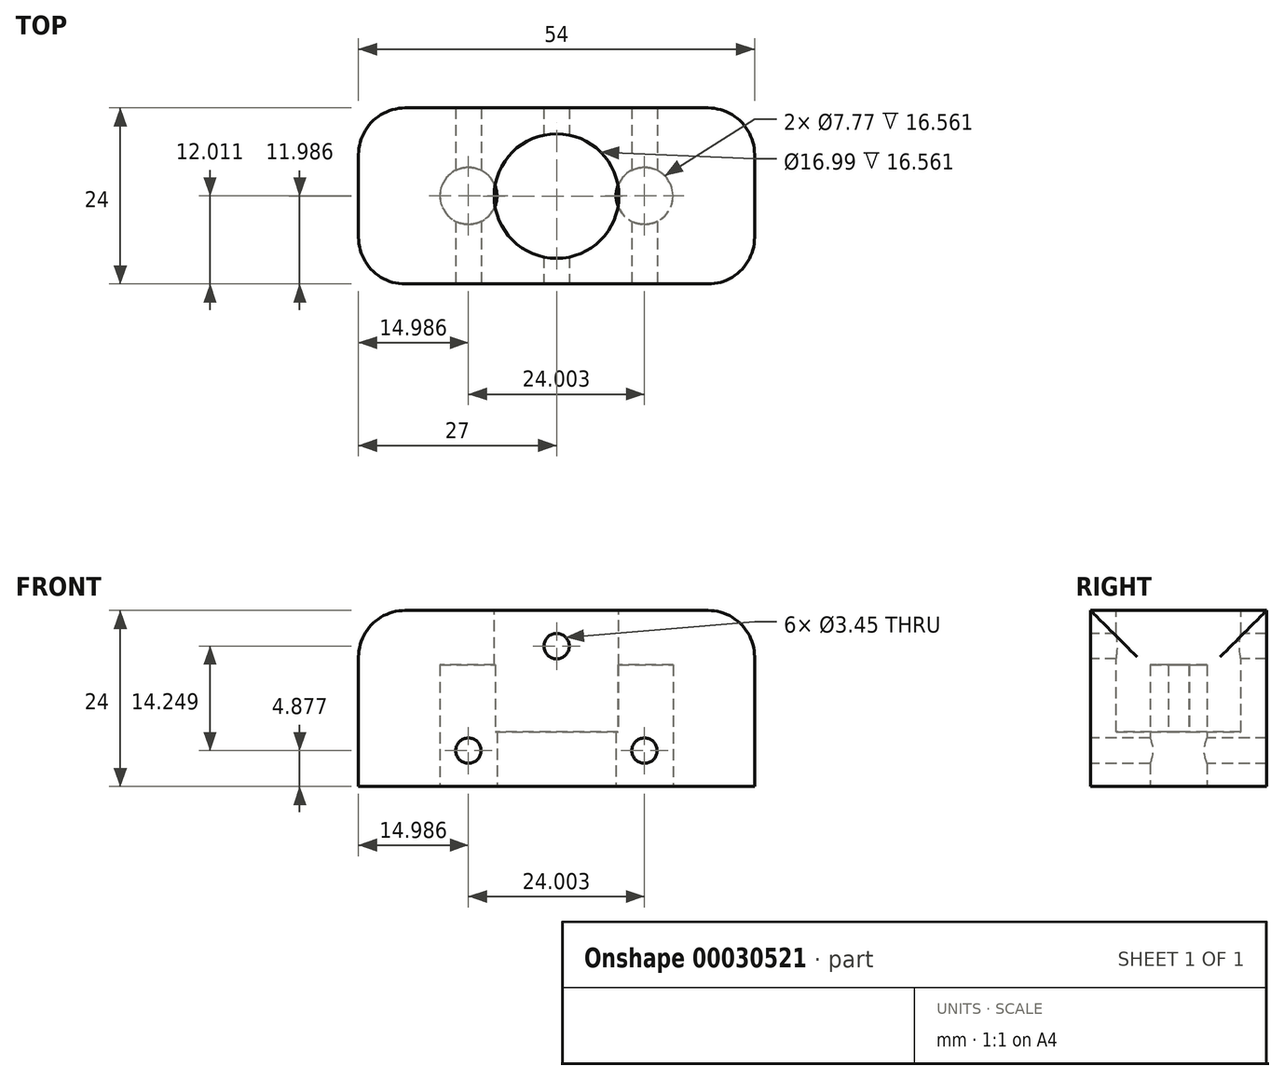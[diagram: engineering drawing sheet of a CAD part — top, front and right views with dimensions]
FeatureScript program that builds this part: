
annotation { "Feature Type Name" : "Feature", "Feature Type Description" : "" }
export const myFeature = defineFeature(function(context is Context, id is Id, definition is map)
    precondition{}
    {
        {
            var Q0;
            Q0=qCreatedBy(makeId("Front.planeOp"),FACE);
            var sketch = newSketch(context, id + "F0", { "sketchPlane" : qUnion([Q0])});
            skLineSegment(sketch, "E0.bottom", {"start": v(0, 0) * mm, "end": v(54, 0) * mm});
            skLineSegment(sketch, "E0.top", {"start": v(0, 24) * mm, "end": v(54, 24) * mm});
            skLineSegment(sketch, "E0.left", {"start": v(0, 0) * mm, "end": v(0, 24) * mm});
            skLineSegment(sketch, "E0.right", {"start": v(54, 0) * mm, "end": v(54, 24) * mm});
            skSolve(sketch);
        }
        {
            var Q0;
            Q0=qSketchRegion(id+"F0",true);
            extrude(context, id + "F1", {"entities" : qUnion([Q0]), "depth" : 24 * mm});
        }
        {
            var Q0;
            Q0=makeQuery(id+"F1.opExtrude","SWEPT_FACE",FACE,{"disambiguationData":[OSD([sQuery(id+"F0.wireOp",EDGE,"E0.top")])]});
            var sketch = newSketch(context, id + "F2", { "sketchPlane" : qUnion([Q0])});
            skCircle(sketch, "E1", {"center": v(27, -12.01) * mm, "radius": 8.5 * mm});
            skSolve(sketch);
        }
        {
            var Q0;
            Q0=qSketchRegion(id+"F2",true);
            extrude(context, id + "F6", {"entities" : qUnion([Q0]), "operationType" : NewBodyOperationType.REMOVE, "oppositeDirection" : true, "depth" : 16.56 * mm});
        }
        {
            var Q0;
            Q0=makeQuery(id+"F1.opExtrude","SWEPT_FACE",FACE,{"disambiguationData":[OSD([sQuery(id+"F0.wireOp",EDGE,"E0.bottom")])]});
            var sketch = newSketch(context, id + "F7", { "sketchPlane" : qUnion([Q0])});
            skCircle(sketch, "E2", {"center": v(14.99, 11.99) * mm, "radius": 3.89 * mm});
            skCircle(sketch, "E3", {"center": v(38.99, 11.99) * mm, "radius": 3.89 * mm});
            skSolve(sketch);
        }
        {
            var Q0;
            Q0=qSketchRegion(id+"F7",true);
            extrude(context, id + "F8", {"entities" : qUnion([Q0]), "operationType" : NewBodyOperationType.REMOVE, "oppositeDirection" : true, "depth" : 16.56 * mm});
        }
        {
            var Q0;
            Q0=makeQuery(id+"F1.opExtrude","SWEPT_EDGE",EDGE,{"disambiguationData":[OSD([sQuery(id+"F0.wireOp",EDGE,"E0.top"),sQuery(id+"F0.wireOp",EDGE,"E0.right")])]});
            var Q1;
            Q1=makeQuery(id+"F1.opExtrude","SWEPT_EDGE",EDGE,{"disambiguationData":[OSD([sQuery(id+"F0.wireOp",EDGE,"E0.top"),sQuery(id+"F0.wireOp",EDGE,"E0.left")])]});
            fillet(context, id + "F3", {"entities" : qUnion([Q0, Q1]), "radius" : 6.35 * mm, "allowEdgeOverflow" : false});
        }
        {
            var Q0;
            Q0=makeQuery(id+"F1.opExtrude","CAP_EDGE",EDGE,{"disambiguationData":[OSD([sQuery(id+"F0.wireOp",EDGE,"E0.right")])],"isStart":false});
            var Q1;
            Q1=makeQuery(id+"F1.opExtrude","CAP_EDGE",EDGE,{"disambiguationData":[OSD([sQuery(id+"F0.wireOp",EDGE,"E0.right")])],"isStart":true});
            var Q2;
            Q2=makeQuery(id+"F1.opExtrude","CAP_EDGE",EDGE,{"disambiguationData":[OSD([sQuery(id+"F0.wireOp",EDGE,"E0.left")])],"isStart":false});
            var Q3;
            Q3=makeQuery(id+"F1.opExtrude","CAP_EDGE",EDGE,{"disambiguationData":[OSD([sQuery(id+"F0.wireOp",EDGE,"E0.left")])],"isStart":true});
            fillet(context, id + "F4", {"entities" : qUnion([Q0, Q1, Q2, Q3]), "radius" : 6.35 * mm, "allowEdgeOverflow" : false});
        }
        {
            var Q0;
            Q0=makeQuery(id+"F1.opExtrude","CAP_FACE",FACE,{"disambiguationData":[OSD([sQuery(id+"F0.wireOp",EDGE,"E0.bottom"),sQuery(id+"F0.wireOp",EDGE,"E0.top"),sQuery(id+"F0.wireOp",EDGE,"E0.left"),sQuery(id+"F0.wireOp",EDGE,"E0.right")])],"isStart":false});
            var sketch = newSketch(context, id + "F9", { "sketchPlane" : qUnion([Q0])});
            skPoint(sketch, "E4", {"position": v(27, 19.13) * mm});
            skPoint(sketch, "E5", {"position": v(14.99, 4.88) * mm});
            skPoint(sketch, "E6", {"position": v(38.99, 4.88) * mm});
            skSolve(sketch);
        }
        {
            var Q0;
            Q0=sQuery(id+"F9.wireOp",VERTEX,"E4");
            var Q1;
            Q1=sQuery(id+"F9.wireOp",VERTEX,"E6");
            var Q2;
            Q2=sQuery(id+"F9.wireOp",VERTEX,"E5");
            var Q3;
            Q3=makeQuery(id+"F1.opExtrude","SWEPT_BODY",BODY,{"disambiguationData":[OSD([sQuery(id+"F0.wireOp",EDGE,"E0.bottom"),sQuery(id+"F0.wireOp",EDGE,"E0.top"),sQuery(id+"F0.wireOp",EDGE,"E0.left"),sQuery(id+"F0.wireOp",EDGE,"E0.right")])]});
            hole(context, id + "F5", {"style" : HoleStyle.SIMPLE, "holeDiameter" : 3.45 * mm, "endStyle" : HoleEndStyle.THROUGH, "locations" : qUnion([Q0, Q1, Q2]), "scope" : qUnion([Q3]), "standardTappedOrClearance" : lookupTablePath({ "standard" : "ANSI", "engagement" : "75%", "pitch" : "32 tpi", "size" : "#8", "type" : "Tapped" }), "standardBlindInLast" : lookupTablePath({ "standard" : "ANSI", "engagement" : "75%", "pitch" : "32 tpi", "size" : "#8", "type" : "Tapped" }), "isTappedThrough" : true, "majorDiameter" : 4.17 * mm, "showTappedDepth" : true});
        }
    });
